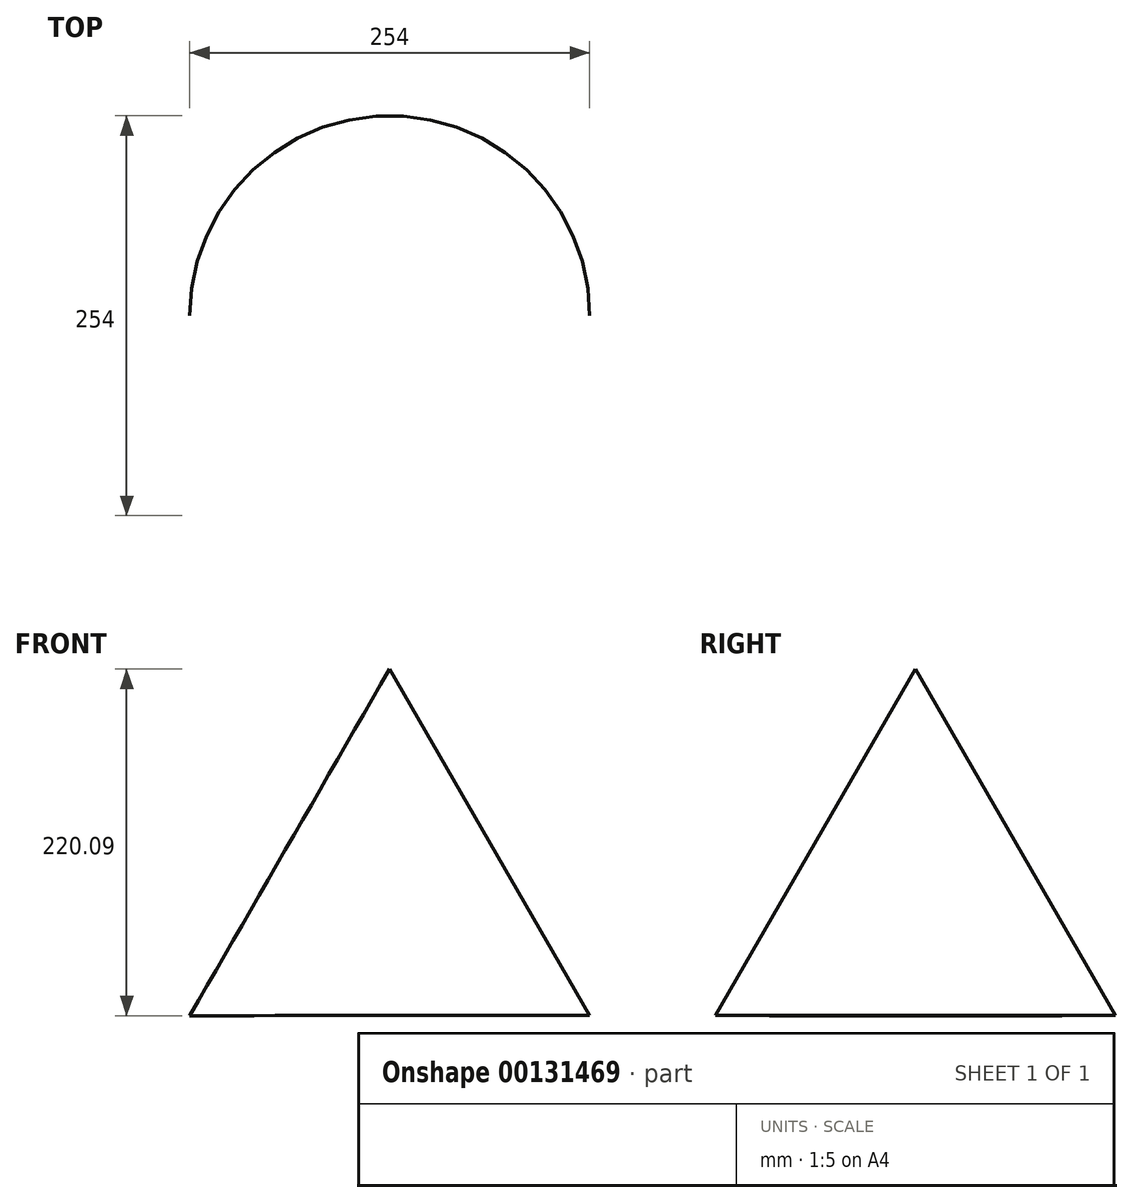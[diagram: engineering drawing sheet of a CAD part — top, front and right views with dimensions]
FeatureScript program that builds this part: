
annotation { "Feature Type Name" : "Feature", "Feature Type Description" : "" }
export const myFeature = defineFeature(function(context is Context, id is Id, definition is map)
    precondition{}
    {
        {
            var Q0;
            Q0=qCreatedBy(makeId("Front.planeOp"),FACE);
            var sketch = newSketch(context, id + "F0", { "sketchPlane" : qUnion([Q0])});
            skCircle(sketch, "E0.cCircle", {"center": v(-13.42, 0) * mm, "radius": 73.32 * mm, "construction": true});
            skLineSegment(sketch, "E0.0", {"start": v(113.65, -73.2) * mm, "end": v(-140.35, -73.44) * mm});
            skLineSegment(sketch, "E0.1", {"start": v(-140.35, -73.44) * mm, "end": v(-13.56, 146.65) * mm});
            skLineSegment(sketch, "E0.2", {"start": v(-13.56, 146.65) * mm, "end": v(113.65, -73.2) * mm});
            skPoint(sketch, "E0.0.midPoint", {"position": v(-13.35, -73.32) * mm});
            skLineSegment(sketch, "E1", {"start": v(-13.56, 146.65) * mm, "end": v(-13.35, -73.32) * mm});
            skSolve(sketch);
        }
        {
            var Q0;
            {var subQ0=sQuery(id+"F0.wireOp",EDGE,"E0.2");Q0=makeQuery(id+"F0.imprint","IMPRINT",FACE,{"disambiguationData":[TD([[makeQuery(id+"F0.imprint","IMPRINT",EDGE,{"derivedFrom":subQ0}),-1.0]])]});}
            var Q1;
            Q1=sQuery(id+"F0.wireOp",EDGE,"E1");
            revolve(context, id + "F1", {"entities" : qUnion([Q0]), "axis" : qUnion([Q1]), "revolveType" : RevolveType.FULL});
        }
    });
